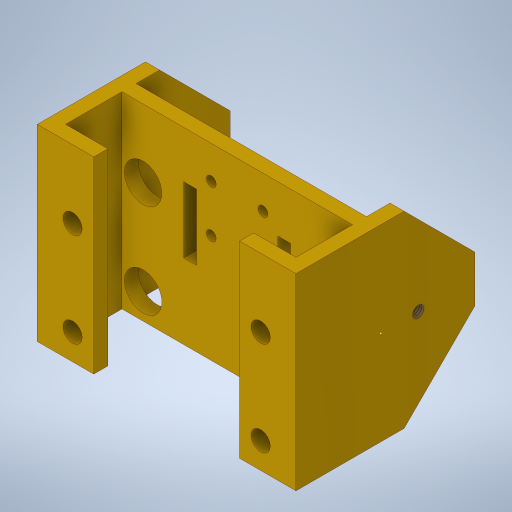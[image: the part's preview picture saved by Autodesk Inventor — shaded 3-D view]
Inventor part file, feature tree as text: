
AUTODESK INVENTOR PART (.ipt)
format: ipt  version: 2024 (Build 280153000, 153)  size: 401,408 bytes
history: native  units: mm
features: extrude x6, hole x4, projected_geometry x3, chamfer x2
ambient origin geometry x8: Origin, YZ Plane, XZ Plane, XY Plane, X Axis, Y Axis, Z Axis, Center Point
bodies: Solid1 (feature_tree)
feature tree (15):
  extrude  "Extrusion1"  Depth=55.0mm
  extrude  "Extrusion2"  Depth=40.0mm
  extrude  "Extrusion3"  Depth=3.0mm TaperAngle=0.0deg
  hole  "Hole1"  [1 undecoded]
  extrude  "Extrusion4"  Depth=3.0mm
  hole  "Hole2"  [1 undecoded]
  extrude  "Extrusion5"  Depth=12.0mm
  chamfer  "Chamfer1"  Distance=12.0mm
  chamfer  "Chamfer2"  Distance=3.0mm
  hole  "Hole3"  [1 undecoded]
  hole  "Hole4"  [1 undecoded]
  extrude  "Extrusion6"  Depth=14.5mm
  projected_geometry  "Projected Loop1"
  projected_geometry  "Projected Loop2"
  projected_geometry  "Projected Loop3"
note: 4 required parameter values undecoded (feature->parameter linkage not recoverable at this tier; creation-order binding heuristic only, values carry confidence <= 0.55)
